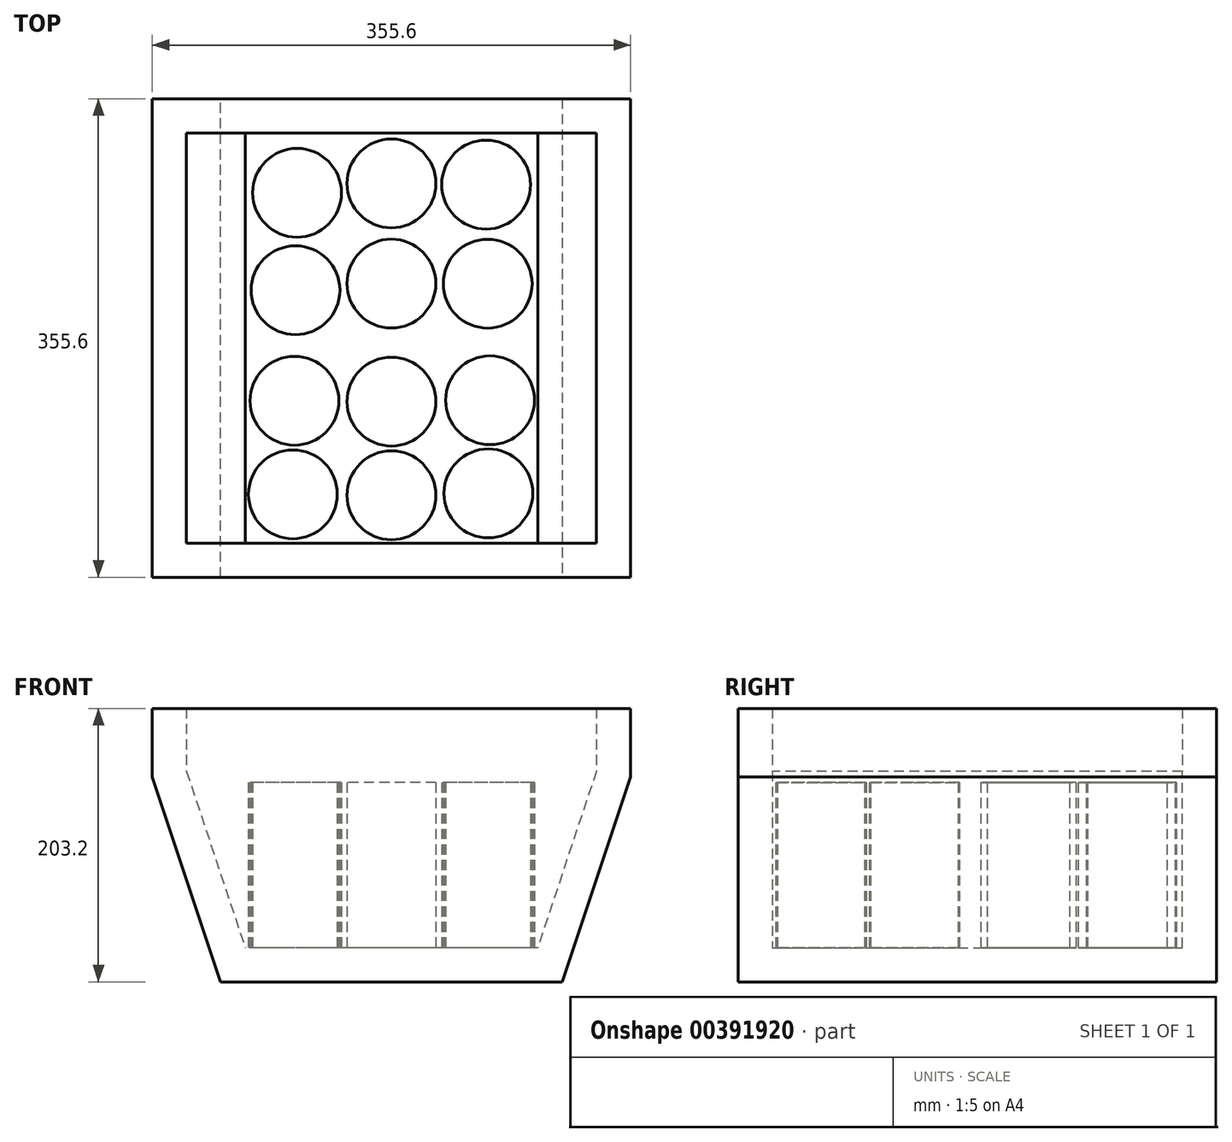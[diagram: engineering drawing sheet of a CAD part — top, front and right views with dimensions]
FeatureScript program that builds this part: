
annotation { "Feature Type Name" : "Feature", "Feature Type Description" : "" }
export const myFeature = defineFeature(function(context is Context, id is Id, definition is map)
    precondition{}
    {
        {
            var Q0;
            Q0=qCreatedBy(makeId("Top.planeOp"),FACE);
            var sketch = newSketch(context, id + "F0", { "sketchPlane" : qUnion([Q0])});
            skLineSegment(sketch, "E0.bottom", {"start": v(177.8, -177.8) * mm, "end": v(-177.8, -177.8) * mm});
            skLineSegment(sketch, "E0.top", {"start": v(177.8, 177.8) * mm, "end": v(-177.8, 177.8) * mm});
            skLineSegment(sketch, "E0.left", {"start": v(177.8, -177.8) * mm, "end": v(177.8, 177.8) * mm});
            skLineSegment(sketch, "E0.right", {"start": v(-177.8, -177.8) * mm, "end": v(-177.8, 177.8) * mm});
            skPoint(sketch, "E0.middle", {"position": v(0, 0) * mm});
            skSolve(sketch);
        }
        {
            var Q0;
            Q0=makeQuery(id+"F0.imprint","IMPRINT",FACE,{"disambiguationData":[TD([[makeQuery(id+"F0.imprint","IMPRINT",EDGE,{"derivedFrom":sQuery(id+"F0.wireOp",EDGE,"E0.bottom")}),-1.0]])]});
            extrude(context, id + "F1", {"entities" : qUnion([Q0]), "depth" : 203.2 * mm});
        }
        {
            var Q0;
            Q0=makeQuery(id+"F1.opExtrude","CAP_EDGE",EDGE,{"disambiguationData":[OSD([sQuery(id+"F0.wireOp",EDGE,"E0.left")])],"isStart":true});
            var Q1;
            Q1=makeQuery(id+"F1.opExtrude","CAP_EDGE",EDGE,{"disambiguationData":[OSD([sQuery(id+"F0.wireOp",EDGE,"E0.right")])],"isStart":true});
            chamfer(context, id + "F2", {"entities" : qUnion([Q0, Q1]), "chamferType" : ChamferType.TWO_OFFSETS, "width1" : 152.4 * mm, "oppositeDirection" : false, "width2" : 50.8 * mm, "tangentPropagation" : true});
        }
        {
            var Q0;
            Q0=makeQuery(id+"F1.opExtrude","CAP_FACE",FACE,{"disambiguationData":[OSD([sQuery(id+"F0.wireOp",EDGE,"E0.bottom"),sQuery(id+"F0.wireOp",EDGE,"E0.top"),sQuery(id+"F0.wireOp",EDGE,"E0.left"),sQuery(id+"F0.wireOp",EDGE,"E0.right")])],"isStart":false});
            shell(context, id + "F3", {"entities" : qUnion([Q0]), "thickness" : 25.4 * mm});
        }
        {
            var Q0;
            Q0=makeQuery(id+"F3.opShell","OFFSET_FACE",FACE,{"disambiguationData":[OSD([sQuery(id+"F0.wireOp",EDGE,"E0.bottom"),sQuery(id+"F0.wireOp",EDGE,"E0.top"),sQuery(id+"F0.wireOp",EDGE,"E0.left"),sQuery(id+"F0.wireOp",EDGE,"E0.right")])]});
            var sketch = newSketch(context, id + "F4", { "sketchPlane" : qUnion([Q0])});
            skCircle(sketch, "E1", {"center": v(-70.2, 107.83) * mm, "radius": 33.02 * mm});
            skSolve(sketch);
        }
        {
            var Q0;
            Q0=makeQuery(id+"F4.imprint","IMPRINT",FACE,{"disambiguationData":[TD([[makeQuery(id+"F4.imprint","IMPRINT",EDGE,{"derivedFrom":sQuery(id+"F4.wireOp",EDGE,"E1")}),1.0]])]});
            extrude(context, id + "F5", {"entities" : qUnion([Q0]), "operationType" : NewBodyOperationType.ADD, "depth" : 122.68 * mm});
        }
        {
            var Q0;
            Q0=makeQuery(id+"F3.opShell","OFFSET_FACE",FACE,{"disambiguationData":[OSD([sQuery(id+"F0.wireOp",EDGE,"E0.bottom"),sQuery(id+"F0.wireOp",EDGE,"E0.top"),sQuery(id+"F0.wireOp",EDGE,"E0.left"),sQuery(id+"F0.wireOp",EDGE,"E0.right")])]});
            var sketch = newSketch(context, id + "F6", { "sketchPlane" : qUnion([Q0])});
            skCircle(sketch, "E2", {"center": v(0, 114.8) * mm, "radius": 33.02 * mm});
            skCircle(sketch, "E3", {"center": v(70.39, 113.93) * mm, "radius": 33.02 * mm});
            skCircle(sketch, "E4", {"center": v(-71.36, 35.45) * mm, "radius": 33.02 * mm});
            skCircle(sketch, "E5", {"center": v(-0.04, 40.37) * mm, "radius": 33.02 * mm});
            skCircle(sketch, "E6", {"center": v(73.29, -46.32) * mm, "radius": 33.02 * mm});
            skCircle(sketch, "E7", {"center": v(72.01, -115.51) * mm, "radius": 33.02 * mm});
            skCircle(sketch, "E8", {"center": v(0, -47.33) * mm, "radius": 33.02 * mm});
            skCircle(sketch, "E9", {"center": v(0, -116.9) * mm, "radius": 33.02 * mm});
            skCircle(sketch, "E10", {"center": v(-72.12, -46.71) * mm, "radius": 33.02 * mm});
            skCircle(sketch, "E11", {"center": v(-73.28, -116.2) * mm, "radius": 33.02 * mm});
            skCircle(sketch, "E12", {"center": v(71.54, 40.3) * mm, "radius": 33.02 * mm});
            skSolve(sketch);
        }
        {
            var Q0;
            Q0=makeQuery(id+"F6.imprint","IMPRINT",FACE,{"disambiguationData":[TD([[makeQuery(id+"F6.imprint","IMPRINT",EDGE,{"derivedFrom":sQuery(id+"F6.wireOp",EDGE,"E2")}),1.0]])]});
            extrude(context, id + "F7", {"entities" : qUnion([Q0]), "operationType" : NewBodyOperationType.ADD, "depth" : 122.68 * mm});
        }
        {
            var Q0;
            Q0=makeQuery(id+"F6.imprint","IMPRINT",FACE,{"disambiguationData":[TD([[makeQuery(id+"F6.imprint","IMPRINT",EDGE,{"derivedFrom":sQuery(id+"F6.wireOp",EDGE,"E2")}),1.0]])]});
            var Q1;
            Q1=makeQuery(id+"F6.imprint","IMPRINT",FACE,{"disambiguationData":[TD([[makeQuery(id+"F6.imprint","IMPRINT",EDGE,{"derivedFrom":sQuery(id+"F6.wireOp",EDGE,"E3")}),1.0]])]});
            var Q2;
            Q2=makeQuery(id+"F6.imprint","IMPRINT",FACE,{"disambiguationData":[TD([[makeQuery(id+"F6.imprint","IMPRINT",EDGE,{"derivedFrom":sQuery(id+"F6.wireOp",EDGE,"E12")}),1.0]])]});
            var Q3;
            Q3=makeQuery(id+"F6.imprint","IMPRINT",FACE,{"disambiguationData":[TD([[makeQuery(id+"F6.imprint","IMPRINT",EDGE,{"derivedFrom":sQuery(id+"F6.wireOp",EDGE,"E5")}),1.0]])]});
            var Q4;
            Q4=makeQuery(id+"F6.imprint","IMPRINT",FACE,{"disambiguationData":[TD([[makeQuery(id+"F6.imprint","IMPRINT",EDGE,{"derivedFrom":sQuery(id+"F6.wireOp",EDGE,"E4")}),1.0]])]});
            var Q5;
            Q5=makeQuery(id+"F6.imprint","IMPRINT",FACE,{"disambiguationData":[TD([[makeQuery(id+"F6.imprint","IMPRINT",EDGE,{"derivedFrom":sQuery(id+"F6.wireOp",EDGE,"E10")}),1.0]])]});
            var Q6;
            Q6=makeQuery(id+"F6.imprint","IMPRINT",FACE,{"disambiguationData":[TD([[makeQuery(id+"F6.imprint","IMPRINT",EDGE,{"derivedFrom":sQuery(id+"F6.wireOp",EDGE,"E8")}),1.0]])]});
            var Q7;
            Q7=makeQuery(id+"F6.imprint","IMPRINT",FACE,{"disambiguationData":[TD([[makeQuery(id+"F6.imprint","IMPRINT",EDGE,{"derivedFrom":sQuery(id+"F6.wireOp",EDGE,"E6")}),1.0]])]});
            var Q8;
            Q8=makeQuery(id+"F6.imprint","IMPRINT",FACE,{"disambiguationData":[TD([[makeQuery(id+"F6.imprint","IMPRINT",EDGE,{"derivedFrom":sQuery(id+"F6.wireOp",EDGE,"E7")}),1.0]])]});
            var Q9;
            Q9=makeQuery(id+"F6.imprint","IMPRINT",FACE,{"disambiguationData":[TD([[makeQuery(id+"F6.imprint","IMPRINT",EDGE,{"derivedFrom":sQuery(id+"F6.wireOp",EDGE,"E9")}),1.0]])]});
            var Q10;
            Q10=makeQuery(id+"F6.imprint","IMPRINT",FACE,{"disambiguationData":[TD([[makeQuery(id+"F6.imprint","IMPRINT",EDGE,{"derivedFrom":sQuery(id+"F6.wireOp",EDGE,"E11")}),1.0]])]});
            extrude(context, id + "F8", {"entities" : qUnion([Q0, Q1, Q2, Q3, Q4, Q5, Q6, Q7, Q8, Q9, Q10]), "operationType" : NewBodyOperationType.ADD, "depth" : 122.68 * mm});
        }
        {
            var Q0;
            Q0=makeQuery(id+"F1.opExtrude","CAP_FACE",FACE,{"disambiguationData":[OSD([sQuery(id+"F0.wireOp",EDGE,"E0.bottom"),sQuery(id+"F0.wireOp",EDGE,"E0.top"),sQuery(id+"F0.wireOp",EDGE,"E0.left"),sQuery(id+"F0.wireOp",EDGE,"E0.right")])],"isStart":false});
            var sketch = newSketch(context, id + "F9", { "sketchPlane" : qUnion([Q0])});
            skLineSegment(sketch, "E13", {"start": v(152.4, -152.4) * mm, "end": v(177.8, -177.8) * mm});
            skSolve(sketch);
        }
        {
            var Q0;
            {var subQ6=sQuery(id+"F0.wireOp",EDGE,"E0.bottom");var subQ7=makeQuery(id+"F1.opExtrude","CAP_EDGE",EDGE,{"disambiguationData":[OSD([subQ6])],"isStart":false});Q0=makeQuery(id+"F9.imprint","IMPRINT",FACE,{"disambiguationData":[TD([[makeQuery(id+"F9.imprint","IMPRINT",EDGE,{"derivedFrom":subQ7}),-1.0]])]});}
            cPlane(context, id + "F10", {"entities" : qUnion([Q0]), "cplaneType" : CPlaneType.OFFSET, "offset" : 0 * mm, "width" : 152.4 * mm, "height" : 152.4 * mm});
        }
    });
